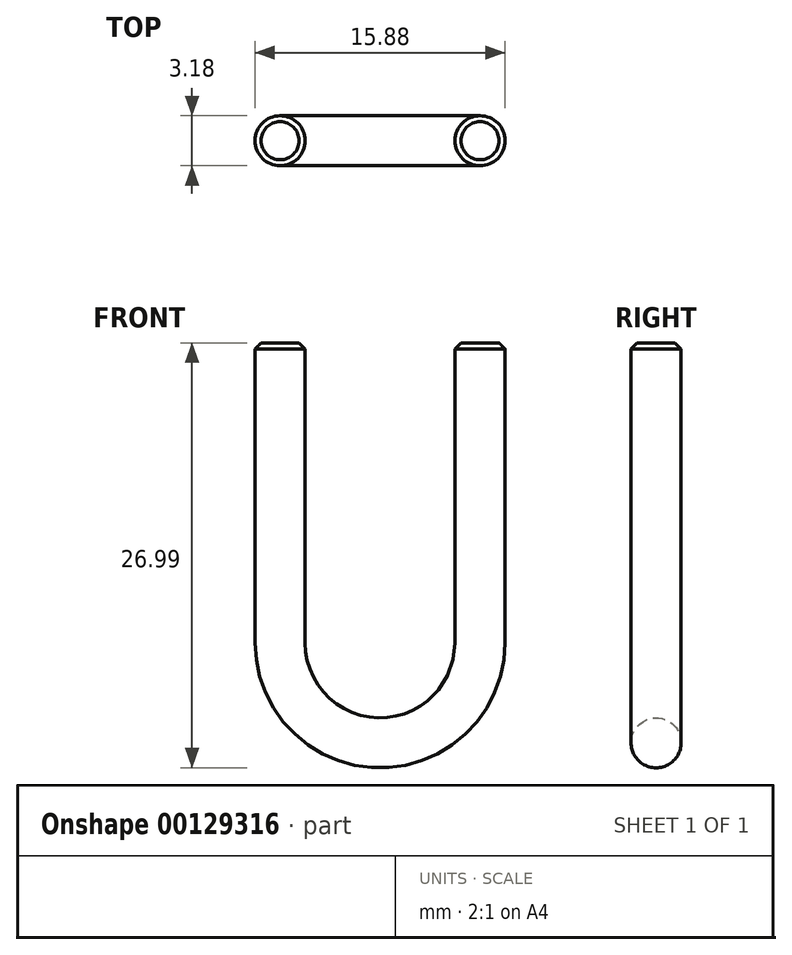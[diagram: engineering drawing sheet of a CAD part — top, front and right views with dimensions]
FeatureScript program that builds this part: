
annotation { "Feature Type Name" : "Feature", "Feature Type Description" : "" }
export const myFeature = defineFeature(function(context is Context, id is Id, definition is map)
    precondition{}
    {
        {
            var Q0;
            Q0=qCreatedBy(makeId("Front.planeOp"),FACE);
            var sketch = newSketch(context, id + "F0", { "sketchPlane" : qUnion([Q0])});
            skArc(sketch, "E0", {"start": v(-6.35, -19.05) * mm, "mid": v(0, -25.4) * mm, "end": v(6.35, -19.05) * mm});
            skLineSegment(sketch, "E1", {"start": v(-6.35, -19.05) * mm, "end": v(-6.35, 0) * mm});
            skLineSegment(sketch, "E2", {"start": v(6.35, -19.05) * mm, "end": v(6.35, 0) * mm});
            skLineSegment(sketch, "E3", {"start": v(-6.35, 0) * mm, "end": v(6.35, 0) * mm, "construction": true});
            skSolve(sketch);
        }
        {
            var Q0;
            Q0=qCreatedBy(makeId("Top.planeOp"),FACE);
            var sketch = newSketch(context, id + "F1", { "sketchPlane" : qUnion([Q0])});
            skCircle(sketch, "E4", {"center": v(6.35, 0) * mm, "radius": 1.59 * mm});
            skSolve(sketch);
        }
        {
            var Q0;
            Q0=makeQuery(id+"F1.imprint","IMPRINT",FACE,{"disambiguationData":[TD([[makeQuery(id+"F1.imprint","IMPRINT",EDGE,{"derivedFrom":sQuery(id+"F1.wireOp",EDGE,"E4")}),1.0]])]});
            var Q1;
            Q1=sQuery(id+"F0.wireOp",EDGE,"E2");
            var Q2;
            Q2=sQuery(id+"F0.wireOp",EDGE,"E0");
            var Q3;
            Q3=sQuery(id+"F0.wireOp",EDGE,"E1");
            sweep(context, id + "F2", {"profiles" : qUnion([Q0]), "path" : qUnion([Q1, Q2, Q3])});
        }
        {
            var Q0;
            Q0=makeQuery(id+"F2.opSweep","CAP_EDGE",EDGE,{"disambiguationData":[OSD([sQuery(id+"F0.wireOp",VERTEX,"E1.end"),sQuery(id+"F1.wireOp",EDGE,"E4")])],"isStart":false});
            var Q1;
            Q1=makeQuery(id+"F2.opSweep","CAP_EDGE",EDGE,{"disambiguationData":[OSD([sQuery(id+"F0.wireOp",VERTEX,"E2.end"),sQuery(id+"F1.wireOp",EDGE,"E4")])],"isStart":true});
            chamfer(context, id + "F3", {"entities" : qUnion([Q0, Q1]), "width" : 0.38 * mm, "tangentPropagation" : true});
        }
    });
